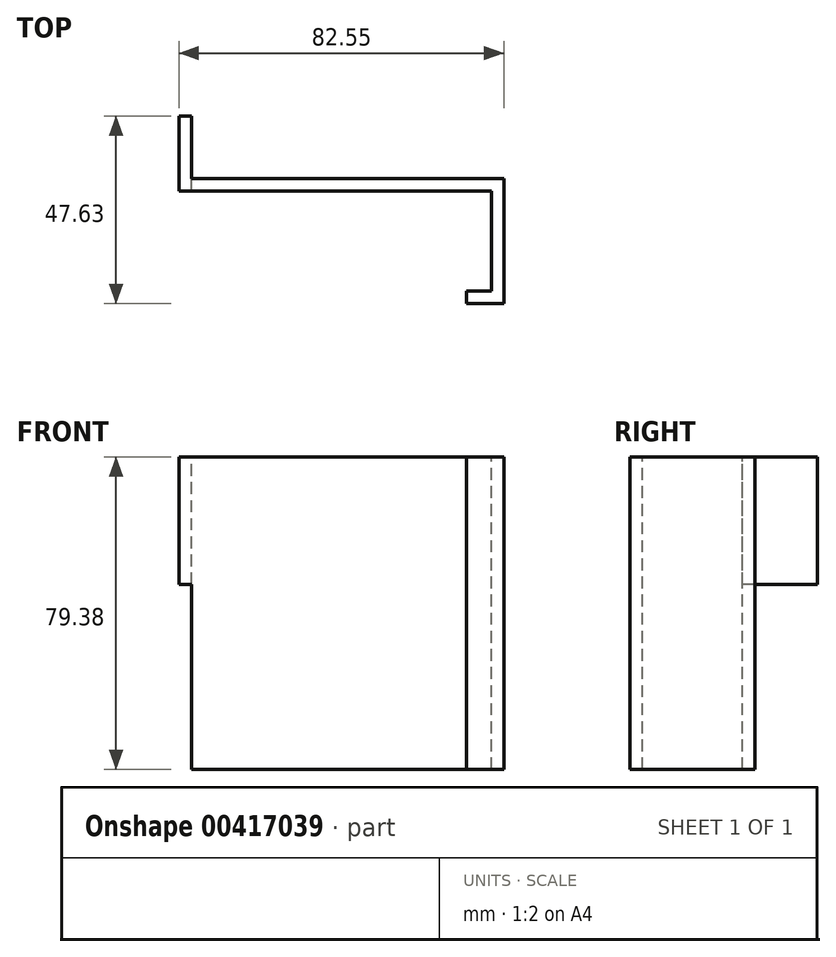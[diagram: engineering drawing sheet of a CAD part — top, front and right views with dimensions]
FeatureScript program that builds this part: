
annotation { "Feature Type Name" : "Feature", "Feature Type Description" : "" }
export const myFeature = defineFeature(function(context is Context, id is Id, definition is map)
    precondition{}
    {
        {
            var Q0;
            Q0=qCreatedBy(makeId("Front.planeOp"),FACE);
            var sketch = newSketch(context, id + "F0", { "sketchPlane" : qUnion([Q0])});
            skLineSegment(sketch, "E0", {"start": v(-41.92, -33.34) * mm, "end": v(-41.92, 42.86) * mm});
            skLineSegment(sketch, "E1", {"start": v(-41.92, -33.34) * mm, "end": v(40.63, -33.34) * mm});
            skLineSegment(sketch, "E2.top", {"start": v(-41.92, 42.86) * mm, "end": v(40.63, 42.86) * mm});
            skLineSegment(sketch, "E2.right", {"start": v(40.63, -33.34) * mm, "end": v(40.63, 42.86) * mm});
            skSolve(sketch);
        }
        {
            var Q0;
            Q0=makeQuery(id+"F0.imprint","IMPRINT",FACE,{"disambiguationData":[TD([[makeQuery(id+"F0.imprint","IMPRINT",EDGE,{"derivedFrom":sQuery(id+"F0.wireOp",EDGE,"E1")}),1.0]])]});
            extrude(context, id + "F1", {"entities" : qUnion([Q0]), "depth" : 31.75 * mm});
        }
        {
            var Q0;
            Q0=makeQuery(id+"F1.opExtrude","SWEPT_FACE",FACE,{"disambiguationData":[OSD([sQuery(id+"F0.wireOp",EDGE,"E2.top")])]});
            var sketch = newSketch(context, id + "F2", { "sketchPlane" : qUnion([Q0])});
            skLineSegment(sketch, "E3", {"start": v(-16.93, 0) * mm, "end": v(-16.93, -3.17) * mm, "construction": true});
            skLineSegment(sketch, "E4", {"start": v(-41.92, -3.17) * mm, "end": v(40.63, -3.17) * mm});
            skLineSegment(sketch, "E5", {"start": v(40.63, -11.67) * mm, "end": v(37.46, -11.67) * mm, "construction": true});
            skLineSegment(sketch, "E6", {"start": v(37.46, 0) * mm, "end": v(37.46, -31.75) * mm});
            skSolve(sketch);
        }
        {
            var Q0;
            {var subQ1=sQuery(id+"F0.wireOp",EDGE,"E2.top");var subQ4=sQuery(id+"F2.wireOp",EDGE,"E6");var subQ6=makeQuery(id+"F1.opExtrude","CAP_EDGE",EDGE,{"disambiguationData":[OSD([subQ1])],"isStart":false});var subQ8=makeQuery(id+"F2.imprint","INTERSECT",VERTEX,{"derivedFrom":[subQ6,subQ4]});Q0=makeQuery(id+"F2.imprint","IMPRINT",FACE,{"disambiguationData":[TD([[makeQuery(id+"F2.imprint","IMPRINT",EDGE,{"disambiguationData":[TD([[subQ8,1.0]])],"derivedFrom":subQ4}),-1.0]])]});}
            extrude(context, id + "F3", {"entities" : qUnion([Q0]), "operationType" : NewBodyOperationType.REMOVE, "oppositeDirection" : true, "depth" : 101.6 * mm});
        }
        {
            var Q0;
            Q0=makeQuery(id+"F1.opExtrude","CAP_FACE",FACE,{"disambiguationData":[OSD([sQuery(id+"F0.wireOp",EDGE,"E1"),sQuery(id+"F0.wireOp",EDGE,"E2.top"),sQuery(id+"F0.wireOp",EDGE,"E0"),sQuery(id+"F0.wireOp",EDGE,"E2.right")])],"isStart":false});
            var sketch = newSketch(context, id + "F4", { "sketchPlane" : qUnion([Q0])});
            skLineSegment(sketch, "E7.bottom", {"start": v(40.63, -33.34) * mm, "end": v(31.1, -33.34) * mm});
            skLineSegment(sketch, "E7.top", {"start": v(40.63, 42.86) * mm, "end": v(31.1, 42.86) * mm});
            skLineSegment(sketch, "E7.left", {"start": v(40.63, -33.34) * mm, "end": v(40.63, 42.86) * mm});
            skLineSegment(sketch, "E7.right", {"start": v(31.1, -33.34) * mm, "end": v(31.1, 42.86) * mm});
            skSolve(sketch);
        }
        {
            var Q0;
            {var subQ2=sQuery(id+"F4.wireOp",EDGE,"E7.right");Q0=makeQuery(id+"F4.imprint","IMPRINT",FACE,{"disambiguationData":[TD([[makeQuery(id+"F4.imprint","IMPRINT",EDGE,{"derivedFrom":subQ2}),-1.0]])]});}
            extrude(context, id + "F5", {"entities" : qUnion([Q0]), "operationType" : NewBodyOperationType.ADD, "oppositeDirection" : true, "depth" : 3.17 * mm});
        }
        {
            var Q0;
            Q0=makeQuery(id+"F5.boolean.opBoolean","MERGE",FACE,{"derivedFrom":[makeQuery(id+"F1.opExtrude","SWEPT_FACE",FACE,{"disambiguationData":[OSD([sQuery(id+"F0.wireOp",EDGE,"E2.top")])]}),makeQuery(id+"F5.opExtrude","SWEPT_FACE",FACE,{"disambiguationData":[OSD([sQuery(id+"F4.wireOp",EDGE,"E7.top")])]})]});
            var sketch = newSketch(context, id + "F6", { "sketchPlane" : qUnion([Q0])});
            skLineSegment(sketch, "E8.bottom", {"start": v(40.63, 0) * mm, "end": v(-41.92, 0) * mm});
            skLineSegment(sketch, "E8.top", {"start": v(40.63, -31.75) * mm, "end": v(-41.92, -31.75) * mm});
            skLineSegment(sketch, "E8.left", {"start": v(40.63, 0) * mm, "end": v(40.63, -31.75) * mm});
            skLineSegment(sketch, "E8.right", {"start": v(-41.92, 0) * mm, "end": v(-41.92, -31.75) * mm});
            skSolve(sketch);
        }
        {
            var Q0;
            {var subQ3=makeQuery(id+"F3.boolean.opBoolean","COPY",EDGE,{"derivedFrom":makeQuery(id+"F3.opExtrude","CAP_EDGE",EDGE,{"disambiguationData":[OSD([sQuery(id+"F2.wireOp",EDGE,"E4")])],"isStart":true})});Q0=makeQuery(id+"F6.imprint","IMPRINT",FACE,{"disambiguationData":[TD([[makeQuery(id+"F6.imprint","IMPRINT",EDGE,{"derivedFrom":subQ3}),-1.0]])]});}
            var Q1;
            {var subQ5=sQuery(id+"F6.wireOp",EDGE,"E8.bottom");Q1=makeQuery(id+"F6.imprint","IMPRINT",FACE,{"disambiguationData":[TD([[makeQuery(id+"F6.imprint","IMPRINT",EDGE,{"derivedFrom":subQ5}),-1.0]])]});}
            extrude(context, id + "F7", {"entities" : qUnion([Q0, Q1]), "operationType" : NewBodyOperationType.ADD, "depth" : 3.17 * mm});
        }
        {
            var Q0;
            Q0=makeQuery(id+"F7.boolean.opBoolean","MERGE",FACE,{"derivedFrom":[makeQuery(id+"F1.opExtrude","SWEPT_FACE",FACE,{"disambiguationData":[OSD([sQuery(id+"F0.wireOp",EDGE,"E0")])]}),makeQuery(id+"F7.opExtrude","SWEPT_FACE",FACE,{"disambiguationData":[OSD([sQuery(id+"F6.wireOp",EDGE,"E8.right")])]})]});
            var sketch = newSketch(context, id + "F8", { "sketchPlane" : qUnion([Q0])});
            skLineSegment(sketch, "E9.bottom", {"start": v(3.17, -33.34) * mm, "end": v(-15.88, -33.34) * mm});
            skLineSegment(sketch, "E9.top", {"start": v(3.17, 46.04) * mm, "end": v(-15.88, 46.04) * mm});
            skLineSegment(sketch, "E9.left", {"start": v(3.17, -33.34) * mm, "end": v(3.17, 46.04) * mm});
            skLineSegment(sketch, "E9.right", {"start": v(-15.88, -33.34) * mm, "end": v(-15.88, 46.04) * mm});
            skSolve(sketch);
        }
        {
            var Q0;
            {var subQ2=sQuery(id+"F8.wireOp",EDGE,"E9.right");Q0=makeQuery(id+"F8.imprint","IMPRINT",FACE,{"disambiguationData":[TD([[makeQuery(id+"F8.imprint","IMPRINT",EDGE,{"derivedFrom":subQ2}),-1.0]])]});}
            extrude(context, id + "F9", {"entities" : qUnion([Q0]), "operationType" : NewBodyOperationType.ADD, "oppositeDirection" : true, "depth" : 3.17 * mm});
        }
        {
            var Q0;
            {var subQ0=sQuery(id+"F6.wireOp",EDGE,"E8.right");var subQ1=sQuery(id+"F0.wireOp",EDGE,"E0");Q0=makeQuery(id+"F9.boolean.opBoolean","MERGE",FACE,{"derivedFrom":[makeQuery(id+"F7.boolean.opBoolean","MERGE",FACE,{"derivedFrom":[makeQuery(id+"F1.opExtrude","SWEPT_FACE",FACE,{"disambiguationData":[OSD([subQ1])]}),makeQuery(id+"F7.opExtrude","SWEPT_FACE",FACE,{"disambiguationData":[OSD([subQ0])]})]}),makeQuery(id+"F9.opExtrude","CAP_FACE",FACE,{"disambiguationData":[OSD([subQ1,sQuery(id+"F6.wireOp",EDGE,"E8.bottom"),subQ0,sQuery(id+"F8.wireOp",EDGE,"E9.bottom"),sQuery(id+"F8.wireOp",EDGE,"E9.top"),sQuery(id+"F8.wireOp",EDGE,"E9.right")])],"isStart":true})]});}
            var sketch = newSketch(context, id + "F10", { "sketchPlane" : qUnion([Q0])});
            skLineSegment(sketch, "E10.bottom", {"start": v(-15.88, -33.34) * mm, "end": v(3.17, -33.34) * mm});
            skLineSegment(sketch, "E10.top", {"start": v(-15.88, 13.65) * mm, "end": v(3.17, 13.65) * mm});
            skLineSegment(sketch, "E10.left", {"start": v(-15.88, -33.34) * mm, "end": v(-15.88, 13.65) * mm});
            skLineSegment(sketch, "E10.right", {"start": v(3.17, -33.34) * mm, "end": v(3.17, 13.65) * mm});
            skSolve(sketch);
        }
        {
            var Q0;
            Q0=makeQuery(id+"F10.imprint","IMPRINT",FACE,{"disambiguationData":[TD([[makeQuery(id+"F10.imprint","IMPRINT",EDGE,{"derivedFrom":sQuery(id+"F10.wireOp",EDGE,"E10.bottom")}),-1.0]])]});
            extrude(context, id + "F11", {"entities" : qUnion([Q0]), "operationType" : NewBodyOperationType.REMOVE, "oppositeDirection" : true, "depth" : 3.17 * mm});
        }
    });
